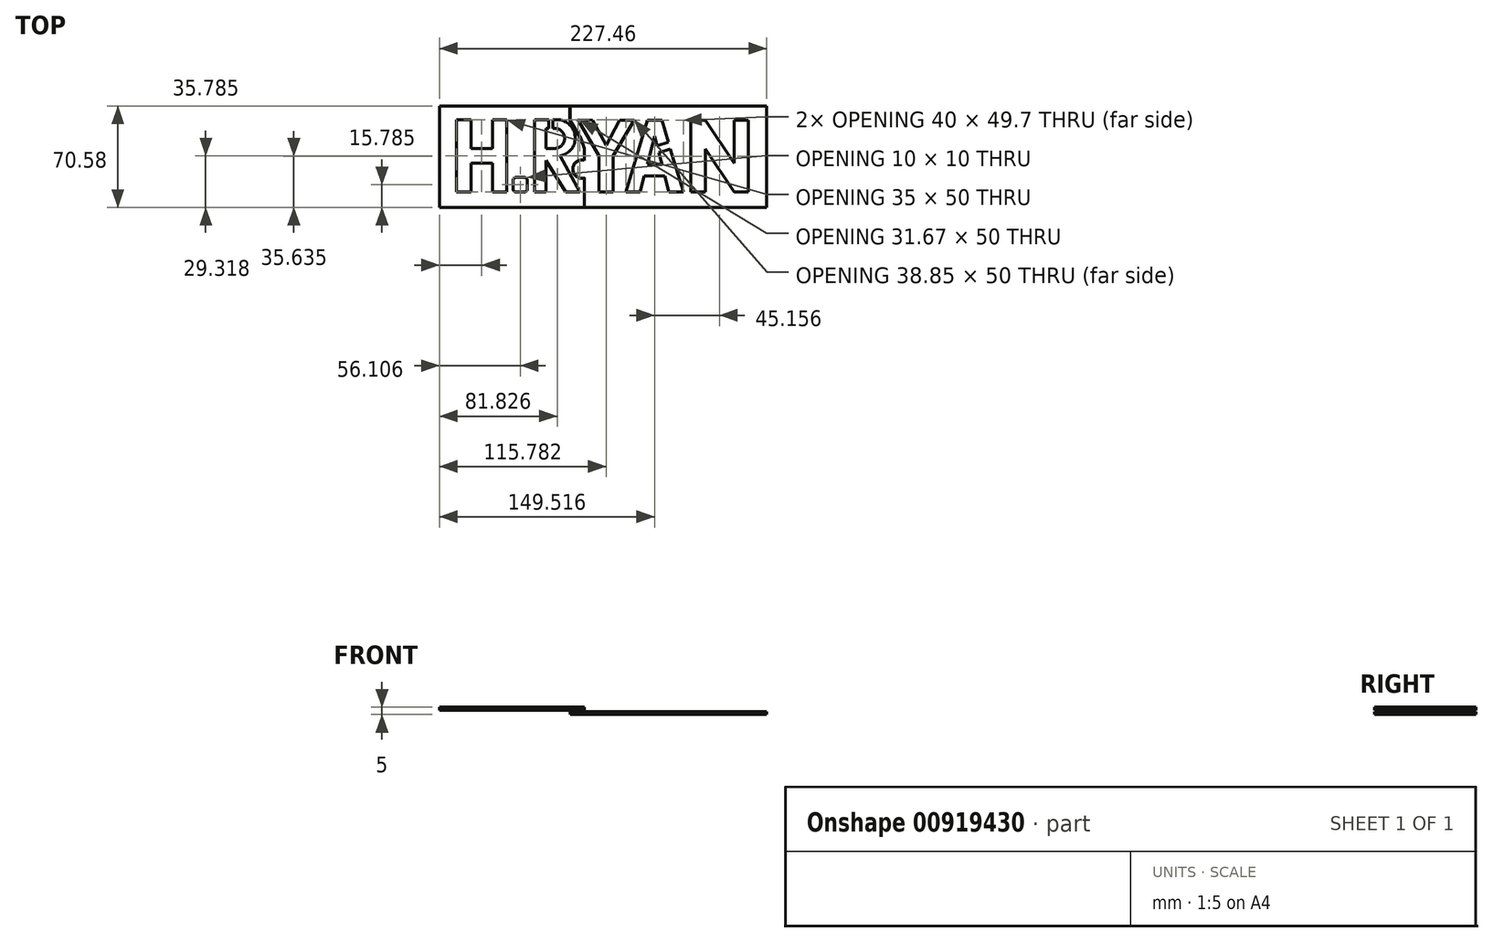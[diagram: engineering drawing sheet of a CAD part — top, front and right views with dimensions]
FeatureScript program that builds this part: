
annotation { "Feature Type Name" : "Feature", "Feature Type Description" : "" }
export const myFeature = defineFeature(function(context is Context, id is Id, definition is map)
    precondition{}
    {
        {
            var Q0;
            Q0=qCreatedBy(makeId("Top.planeOp"),FACE);
            var sketch = newSketch(context, id + "F0", { "sketchPlane" : qUnion([Q0])});
            skLineSegment(sketch, "E0", {"start": v(-56.97, 28.07) * mm, "end": v(-46.97, 28.07) * mm});
            skLineSegment(sketch, "E1", {"start": v(-56.97, 28.07) * mm, "end": v(-56.97, -21.93) * mm});
            skLineSegment(sketch, "E2", {"start": v(-56.97, -21.93) * mm, "end": v(-46.97, -21.93) * mm});
            skLineSegment(sketch, "E3", {"start": v(-46.97, -21.93) * mm, "end": v(-46.97, -1.93) * mm});
            skLineSegment(sketch, "E4", {"start": v(-46.97, 28.07) * mm, "end": v(-46.97, 8.07) * mm});
            skLineSegment(sketch, "E5", {"start": v(-46.97, 8.07) * mm, "end": v(-31.97, 8.07) * mm});
            skLineSegment(sketch, "E6", {"start": v(-46.97, -1.93) * mm, "end": v(-31.97, -1.93) * mm});
            skLineSegment(sketch, "E7", {"start": v(-31.97, -1.93) * mm, "end": v(-31.97, -21.93) * mm});
            skLineSegment(sketch, "E8", {"start": v(-31.97, -21.93) * mm, "end": v(-21.97, -21.93) * mm});
            skLineSegment(sketch, "E9", {"start": v(-21.97, -21.93) * mm, "end": v(-21.97, 28.07) * mm});
            skLineSegment(sketch, "E10", {"start": v(-21.97, 28.07) * mm, "end": v(-31.97, 28.07) * mm});
            skLineSegment(sketch, "E11", {"start": v(-31.97, 28.07) * mm, "end": v(-31.97, 8.07) * mm});
            skLineSegment(sketch, "E12", {"start": v(-15.68, -21.93) * mm, "end": v(-9.68, -21.93) * mm});
            skLineSegment(sketch, "E13", {"start": v(-7.68, -19.93) * mm, "end": v(-7.68, -13.93) * mm});
            skLineSegment(sketch, "E14", {"start": v(-9.68, -11.93) * mm, "end": v(-15.68, -11.93) * mm});
            skLineSegment(sketch, "E15", {"start": v(-17.68, -13.93) * mm, "end": v(-17.68, -19.93) * mm});
            skPoint(sketch, "E16.visualSharp", {"position": v(-17.68, -11.93) * mm});
            skArc(sketch, "E16.filletArc", {"start": v(-15.68, -11.93) * mm, "mid": v(-17.1, -12.52) * mm, "end": v(-17.68, -13.93) * mm});
            skPoint(sketch, "E17.visualSharp", {"position": v(-7.68, -11.93) * mm});
            skArc(sketch, "E17.filletArc", {"start": v(-7.68, -13.93) * mm, "mid": v(-8.27, -12.52) * mm, "end": v(-9.68, -11.93) * mm});
            skPoint(sketch, "E18.visualSharp", {"position": v(-7.68, -21.93) * mm});
            skArc(sketch, "E18.filletArc", {"start": v(-9.68, -21.93) * mm, "mid": v(-8.27, -21.35) * mm, "end": v(-7.68, -19.93) * mm});
            skPoint(sketch, "E19.visualSharp", {"position": v(-17.68, -21.93) * mm});
            skArc(sketch, "E19.filletArc", {"start": v(-17.68, -19.93) * mm, "mid": v(-17.1, -21.35) * mm, "end": v(-15.68, -21.93) * mm});
            skLineSegment(sketch, "E20", {"start": v(0, 28.07) * mm, "end": v(0, -21.93) * mm});
            skLineSegment(sketch, "E21", {"start": v(0, -21.93) * mm, "end": v(8, -21.93) * mm});
            skLineSegment(sketch, "E22", {"start": v(8, -21.93) * mm, "end": v(8, 0) * mm});
            skLineSegment(sketch, "E23", {"start": v(21.67, -21.93) * mm, "end": v(31.67, -21.93) * mm});
            skLineSegment(sketch, "E24", {"start": v(31.67, -21.93) * mm, "end": v(18, 3.07) * mm});
            skLineSegment(sketch, "E25", {"start": v(0, 28.07) * mm, "end": v(10, 28.07) * mm});
            skArc(sketch, "E26", {"start": v(18, 3.07) * mm, "mid": v(28.33, 15.57) * mm, "end": v(18, 28.07) * mm});
            skLineSegment(sketch, "E27", {"start": v(18, 28.07) * mm, "end": v(0, 28.07) * mm});
            skLineSegment(sketch, "E28", {"start": v(8, 8.24) * mm, "end": v(8, 22.3) * mm});
            skLineSegment(sketch, "E29", {"start": v(8, 22.3) * mm, "end": v(14, 22.3) * mm});
            skLineSegment(sketch, "E30", {"start": v(8, 8.24) * mm, "end": v(14, 8.24) * mm});
            skArc(sketch, "E31", {"start": v(14, 8.24) * mm, "mid": v(21.02, 15.27) * mm, "end": v(14, 22.3) * mm});
            skPoint(sketch, "E32.endSnap0", {"position": v(26.67, -21.93) * mm});
            skLineSegment(sketch, "E33", {"start": v(44.8, -21.93) * mm, "end": v(44.8, 3.07) * mm});
            skLineSegment(sketch, "E34", {"start": v(44.8, -21.93) * mm, "end": v(54.8, -21.93) * mm});
            skLineSegment(sketch, "E35", {"start": v(54.8, -21.93) * mm, "end": v(54.8, 3.07) * mm});
            skLineSegment(sketch, "E36", {"start": v(44.8, 3.07) * mm, "end": v(30.37, 28.07) * mm});
            skLineSegment(sketch, "E37", {"start": v(30.37, 28.07) * mm, "end": v(40.37, 27.91) * mm});
            skLineSegment(sketch, "E38", {"start": v(40.37, 27.91) * mm, "end": v(49.8, 10.57) * mm});
            skLineSegment(sketch, "E39", {"start": v(49.8, 27.91) * mm, "end": v(59.22, 27.76) * mm});
            skLineSegment(sketch, "E40", {"start": v(49.8, 10.57) * mm, "end": v(59.22, 27.76) * mm});
            skLineSegment(sketch, "E41", {"start": v(59.22, 27.76) * mm, "end": v(69.22, 27.76) * mm});
            skLineSegment(sketch, "E42", {"start": v(54.8, 3.07) * mm, "end": v(69.22, 27.76) * mm});
            skPoint(sketch, "E43.start.orphan", {"position": v(49.8, -21.93) * mm});
            skLineSegment(sketch, "E44", {"start": v(71.83, -21.93) * mm, "end": v(81.83, -21.93) * mm});
            skLineSegment(sketch, "E45", {"start": v(101.83, -21.93) * mm, "end": v(111.83, -21.93) * mm});
            skLineSegment(sketch, "E46", {"start": v(96.83, 27.76) * mm, "end": v(91.83, 27.76) * mm});
            skLineSegment(sketch, "E47", {"start": v(91.83, 27.76) * mm, "end": v(86.83, 27.76) * mm});
            skLineSegment(sketch, "E48", {"start": v(86.83, 27.76) * mm, "end": v(71.83, -21.93) * mm});
            skLineSegment(sketch, "E49", {"start": v(96.83, 27.76) * mm, "end": v(111.83, -21.93) * mm});
            skLineSegment(sketch, "E50", {"start": v(91.83, 16.9) * mm, "end": v(86.83, -2.52) * mm});
            skLineSegment(sketch, "E51", {"start": v(101.83, -21.93) * mm, "end": v(98.96, -10.8) * mm});
            skLineSegment(sketch, "E52", {"start": v(84.7, -10.8) * mm, "end": v(98.96, -10.8) * mm});
            skLineSegment(sketch, "E53", {"start": v(86.83, -2.52) * mm, "end": v(96.83, -2.52) * mm});
            skPoint(sketch, "E54.orphan", {"position": v(91.83, -21.93) * mm});
            skLineSegment(sketch, "E55.trimOffspring", {"start": v(84.7, -10.8) * mm, "end": v(81.83, -21.93) * mm});
            skLineSegment(sketch, "E56.trimOffspring", {"start": v(96.83, -2.52) * mm, "end": v(91.83, 16.9) * mm});
            skLineSegment(sketch, "E57", {"start": v(21.67, -21.93) * mm, "end": v(8, 0) * mm});
            skPoint(sketch, "E58.orphan", {"position": v(8, 3.07) * mm});
            skLineSegment(sketch, "E59", {"start": v(116.98, -21.93) * mm, "end": v(116.98, 27.76) * mm});
            skLineSegment(sketch, "E60", {"start": v(116.98, 27.76) * mm, "end": v(126.98, 27.76) * mm});
            skLineSegment(sketch, "E61", {"start": v(116.98, -21.93) * mm, "end": v(126.98, -21.93) * mm});
            skLineSegment(sketch, "E62", {"start": v(126.98, 7.76) * mm, "end": v(146.98, -21.93) * mm});
            skLineSegment(sketch, "E63", {"start": v(126.98, 7.76) * mm, "end": v(126.98, -21.93) * mm});
            skLineSegment(sketch, "E64", {"start": v(146.98, -1.93) * mm, "end": v(146.98, 27.76) * mm});
            skLineSegment(sketch, "E65", {"start": v(146.98, -1.93) * mm, "end": v(126.98, 27.76) * mm});
            skLineSegment(sketch, "E66", {"start": v(146.98, 27.76) * mm, "end": v(156.98, 27.76) * mm});
            skLineSegment(sketch, "E67", {"start": v(156.98, 27.76) * mm, "end": v(156.98, -21.93) * mm});
            skLineSegment(sketch, "E68", {"start": v(156.98, -21.93) * mm, "end": v(146.98, -21.93) * mm});
            skSolve(sketch);
        }
        {
            var Q0;
            Q0=makeQuery(id+"F0.imprint","IMPRINT",FACE,{"disambiguationData":[TD([[makeQuery(id+"F0.imprint","IMPRINT",EDGE,{"derivedFrom":sQuery(id+"F0.wireOp",EDGE,"E0")}),-1.0]])]});
            var Q1;
            {var subQ1=sQuery(id+"F0.wireOp",EDGE,"E20");Q1=makeQuery(id+"F0.imprint","IMPRINT",FACE,{"disambiguationData":[TD([[makeQuery(id+"F0.imprint","IMPRINT",EDGE,{"derivedFrom":subQ1}),1.0]])]});}
            var Q2;
            Q2=makeQuery(id+"F0.imprint","IMPRINT",FACE,{"disambiguationData":[TD([[makeQuery(id+"F0.imprint","IMPRINT",EDGE,{"derivedFrom":sQuery(id+"F0.wireOp",EDGE,"E12")}),1.0]])]});
            var Q3;
            Q3=makeQuery(id+"F0.imprint","IMPRINT",FACE,{"disambiguationData":[TD([[makeQuery(id+"F0.imprint","IMPRINT",EDGE,{"derivedFrom":sQuery(id+"F0.wireOp",EDGE,"E33")}),-1.0]])]});
            var Q4;
            Q4=makeQuery(id+"F0.imprint","IMPRINT",FACE,{"disambiguationData":[TD([[makeQuery(id+"F0.imprint","IMPRINT",EDGE,{"derivedFrom":sQuery(id+"F0.wireOp",EDGE,"E44")}),1.0]])]});
            var Q5;
            Q5=makeQuery(id+"F0.imprint","IMPRINT",FACE,{"disambiguationData":[TD([[makeQuery(id+"F0.imprint","IMPRINT",EDGE,{"derivedFrom":sQuery(id+"F0.wireOp",EDGE,"E59")}),-1.0]])]});
            extrude(context, id + "F1", {"entities" : qUnion([Q0, Q1, Q2, Q3, Q4, Q5]), "depth" : 25 * mm, "offsetDistance" : 25 * mm});
        }
        {
            var Q0;
            Q0=makeQuery(id+"F1.opExtrude","SWEPT_BODY",BODY,{"disambiguationData":[OSD([sQuery(id+"F0.wireOp",EDGE,"E44"),sQuery(id+"F0.wireOp",EDGE,"E45"),sQuery(id+"F0.wireOp",EDGE,"E46"),sQuery(id+"F0.wireOp",EDGE,"E47"),sQuery(id+"F0.wireOp",EDGE,"E48"),sQuery(id+"F0.wireOp",EDGE,"E49"),sQuery(id+"F0.wireOp",EDGE,"E50"),sQuery(id+"F0.wireOp",EDGE,"E51"),sQuery(id+"F0.wireOp",EDGE,"E52"),sQuery(id+"F0.wireOp",EDGE,"E53"),sQuery(id+"F0.wireOp",EDGE,"E55.trimOffspring"),sQuery(id+"F0.wireOp",EDGE,"E56.trimOffspring")])]});
            var Q1;
            Q1=makeQuery(id+"F1.opExtrude","SWEPT_BODY",BODY,{"disambiguationData":[OSD([sQuery(id+"F0.wireOp",EDGE,"E59"),sQuery(id+"F0.wireOp",EDGE,"E60"),sQuery(id+"F0.wireOp",EDGE,"E61"),sQuery(id+"F0.wireOp",EDGE,"E62"),sQuery(id+"F0.wireOp",EDGE,"E63"),sQuery(id+"F0.wireOp",EDGE,"E64"),sQuery(id+"F0.wireOp",EDGE,"E65"),sQuery(id+"F0.wireOp",EDGE,"E66"),sQuery(id+"F0.wireOp",EDGE,"E67"),sQuery(id+"F0.wireOp",EDGE,"E68")])]});
            transform(context, id + "F2", {"entities" : qUnion([Q0, Q1]), "transformType" : TransformType.TRANSLATION_3D, "dx" : -8.3 * mm, "dy" : 0 * mm, "dz" : 0 * mm, "makeCopy" : false});
        }
        {
            var Q0;
            Q0=makeQuery(id+"F1.opExtrude","SWEPT_BODY",BODY,{"disambiguationData":[OSD([sQuery(id+"F0.wireOp",EDGE,"E33"),sQuery(id+"F0.wireOp",EDGE,"E34"),sQuery(id+"F0.wireOp",EDGE,"E35"),sQuery(id+"F0.wireOp",EDGE,"E36"),sQuery(id+"F0.wireOp",EDGE,"E37"),sQuery(id+"F0.wireOp",EDGE,"E38"),sQuery(id+"F0.wireOp",EDGE,"E40"),sQuery(id+"F0.wireOp",EDGE,"E41"),sQuery(id+"F0.wireOp",EDGE,"E42")])]});
            var Q1;
            Q1=makeQuery(id+"F1.opExtrude","SWEPT_BODY",BODY,{"disambiguationData":[OSD([sQuery(id+"F0.wireOp",EDGE,"E44"),sQuery(id+"F0.wireOp",EDGE,"E45"),sQuery(id+"F0.wireOp",EDGE,"E46"),sQuery(id+"F0.wireOp",EDGE,"E47"),sQuery(id+"F0.wireOp",EDGE,"E48"),sQuery(id+"F0.wireOp",EDGE,"E49"),sQuery(id+"F0.wireOp",EDGE,"E50"),sQuery(id+"F0.wireOp",EDGE,"E51"),sQuery(id+"F0.wireOp",EDGE,"E52"),sQuery(id+"F0.wireOp",EDGE,"E53"),sQuery(id+"F0.wireOp",EDGE,"E55.trimOffspring"),sQuery(id+"F0.wireOp",EDGE,"E56.trimOffspring")])]});
            var Q2;
            Q2=makeQuery(id+"F1.opExtrude","SWEPT_BODY",BODY,{"disambiguationData":[OSD([sQuery(id+"F0.wireOp",EDGE,"E59"),sQuery(id+"F0.wireOp",EDGE,"E60"),sQuery(id+"F0.wireOp",EDGE,"E61"),sQuery(id+"F0.wireOp",EDGE,"E62"),sQuery(id+"F0.wireOp",EDGE,"E63"),sQuery(id+"F0.wireOp",EDGE,"E64"),sQuery(id+"F0.wireOp",EDGE,"E65"),sQuery(id+"F0.wireOp",EDGE,"E66"),sQuery(id+"F0.wireOp",EDGE,"E67"),sQuery(id+"F0.wireOp",EDGE,"E68")])]});
            var Q3;
            Q3=makeQuery(id+"F1.opExtrude","SWEPT_BODY",BODY,{"disambiguationData":[OSD([sQuery(id+"F0.wireOp",EDGE,"E20"),sQuery(id+"F0.wireOp",EDGE,"E21"),sQuery(id+"F0.wireOp",EDGE,"E22"),sQuery(id+"F0.wireOp",EDGE,"E23"),sQuery(id+"F0.wireOp",EDGE,"E24"),sQuery(id+"F0.wireOp",EDGE,"E26"),sQuery(id+"F0.wireOp",EDGE,"E27"),sQuery(id+"F0.wireOp",EDGE,"E28"),sQuery(id+"F0.wireOp",EDGE,"E29"),sQuery(id+"F0.wireOp",EDGE,"E30"),sQuery(id+"F0.wireOp",EDGE,"E31"),sQuery(id+"F0.wireOp",EDGE,"E57")])]});
            transform(context, id + "F3", {"entities" : qUnion([Q0, Q1, Q2, Q3]), "transformType" : TransformType.TRANSLATION_3D, "dx" : -2.8 * mm, "dy" : 0 * mm, "dz" : 0 * mm, "makeCopy" : false});
        }
        {
            var Q0;
            Q0=qCreatedBy(makeId("Top.planeOp"),FACE);
            var sketch = newSketch(context, id + "F4", { "sketchPlane" : qUnion([Q0])});
            skLineSegment(sketch, "E69.bottom", {"start": v(-68.8, 37.86) * mm, "end": v(158.67, 37.86) * mm});
            skLineSegment(sketch, "E69.top", {"start": v(-68.8, -32.72) * mm, "end": v(158.67, -32.72) * mm});
            skLineSegment(sketch, "E69.left", {"start": v(-68.8, 37.86) * mm, "end": v(-68.8, -32.72) * mm});
            skLineSegment(sketch, "E69.right", {"start": v(158.67, 37.86) * mm, "end": v(158.67, -32.72) * mm});
            skSolve(sketch);
        }
        {
            var Q0;
            Q0=makeQuery(id+"F4.imprint","IMPRINT",FACE,{"disambiguationData":[TD([[makeQuery(id+"F4.imprint","IMPRINT",EDGE,{"derivedFrom":sQuery(id+"F4.wireOp",EDGE,"E69.bottom")}),-1.0]])]});
            extrude(context, id + "F5", {"entities" : qUnion([Q0]), "operationType" : NewBodyOperationType.ADD, "depth" : 20 * mm, "offsetDistance" : 25 * mm});
        }
        {
            var Q0;
            Q0=makeQuery(id+"F1.opExtrude","CAP_FACE",FACE,{"disambiguationData":[OSD([sQuery(id+"F0.wireOp",EDGE,"E0"),sQuery(id+"F0.wireOp",EDGE,"E1"),sQuery(id+"F0.wireOp",EDGE,"E2"),sQuery(id+"F0.wireOp",EDGE,"E3"),sQuery(id+"F0.wireOp",EDGE,"E4"),sQuery(id+"F0.wireOp",EDGE,"E5"),sQuery(id+"F0.wireOp",EDGE,"E6"),sQuery(id+"F0.wireOp",EDGE,"E7"),sQuery(id+"F0.wireOp",EDGE,"E8"),sQuery(id+"F0.wireOp",EDGE,"E9"),sQuery(id+"F0.wireOp",EDGE,"E10"),sQuery(id+"F0.wireOp",EDGE,"E11")])],"isStart":false});
            var Q1;
            Q1=makeQuery(id+"F1.opExtrude","CAP_FACE",FACE,{"disambiguationData":[OSD([sQuery(id+"F0.wireOp",EDGE,"E12"),sQuery(id+"F0.wireOp",EDGE,"E13"),sQuery(id+"F0.wireOp",EDGE,"E14"),sQuery(id+"F0.wireOp",EDGE,"E15"),sQuery(id+"F0.wireOp",EDGE,"E16.filletArc"),sQuery(id+"F0.wireOp",EDGE,"E17.filletArc"),sQuery(id+"F0.wireOp",EDGE,"E18.filletArc"),sQuery(id+"F0.wireOp",EDGE,"E19.filletArc")])],"isStart":false});
            var Q2;
            Q2=makeQuery(id+"F1.opExtrude","CAP_FACE",FACE,{"disambiguationData":[OSD([sQuery(id+"F0.wireOp",EDGE,"E20"),sQuery(id+"F0.wireOp",EDGE,"E21"),sQuery(id+"F0.wireOp",EDGE,"E22"),sQuery(id+"F0.wireOp",EDGE,"E23"),sQuery(id+"F0.wireOp",EDGE,"E24"),sQuery(id+"F0.wireOp",EDGE,"E26"),sQuery(id+"F0.wireOp",EDGE,"E27"),sQuery(id+"F0.wireOp",EDGE,"E28"),sQuery(id+"F0.wireOp",EDGE,"E29"),sQuery(id+"F0.wireOp",EDGE,"E30"),sQuery(id+"F0.wireOp",EDGE,"E31"),sQuery(id+"F0.wireOp",EDGE,"E57")])],"isStart":false});
            var Q3;
            Q3=makeQuery(id+"F1.opExtrude","CAP_FACE",FACE,{"disambiguationData":[OSD([sQuery(id+"F0.wireOp",EDGE,"E33"),sQuery(id+"F0.wireOp",EDGE,"E34"),sQuery(id+"F0.wireOp",EDGE,"E35"),sQuery(id+"F0.wireOp",EDGE,"E36"),sQuery(id+"F0.wireOp",EDGE,"E37"),sQuery(id+"F0.wireOp",EDGE,"E38"),sQuery(id+"F0.wireOp",EDGE,"E40"),sQuery(id+"F0.wireOp",EDGE,"E41"),sQuery(id+"F0.wireOp",EDGE,"E42")])],"isStart":false});
            var Q4;
            Q4=makeQuery(id+"F1.opExtrude","CAP_FACE",FACE,{"disambiguationData":[OSD([sQuery(id+"F0.wireOp",EDGE,"E44"),sQuery(id+"F0.wireOp",EDGE,"E45"),sQuery(id+"F0.wireOp",EDGE,"E46"),sQuery(id+"F0.wireOp",EDGE,"E47"),sQuery(id+"F0.wireOp",EDGE,"E48"),sQuery(id+"F0.wireOp",EDGE,"E49"),sQuery(id+"F0.wireOp",EDGE,"E50"),sQuery(id+"F0.wireOp",EDGE,"E51"),sQuery(id+"F0.wireOp",EDGE,"E52"),sQuery(id+"F0.wireOp",EDGE,"E53"),sQuery(id+"F0.wireOp",EDGE,"E55.trimOffspring"),sQuery(id+"F0.wireOp",EDGE,"E56.trimOffspring")])],"isStart":false});
            var Q5;
            Q5=makeQuery(id+"F1.opExtrude","CAP_FACE",FACE,{"disambiguationData":[OSD([sQuery(id+"F0.wireOp",EDGE,"E59"),sQuery(id+"F0.wireOp",EDGE,"E60"),sQuery(id+"F0.wireOp",EDGE,"E61"),sQuery(id+"F0.wireOp",EDGE,"E62"),sQuery(id+"F0.wireOp",EDGE,"E63"),sQuery(id+"F0.wireOp",EDGE,"E64"),sQuery(id+"F0.wireOp",EDGE,"E65"),sQuery(id+"F0.wireOp",EDGE,"E66"),sQuery(id+"F0.wireOp",EDGE,"E67"),sQuery(id+"F0.wireOp",EDGE,"E68")])],"isStart":false});
            extrude(context, id + "F6", {"entities" : qUnion([Q0, Q1, Q2, Q3, Q4, Q5]), "operationType" : NewBodyOperationType.REMOVE, "oppositeDirection" : true, "depth" : 60.1 * mm, "offsetDistance" : 25 * mm});
        }
        {
            var Q0;
            Q0=qCreatedBy(makeId("Top.planeOp"),FACE);
            var sketch = newSketch(context, id + "F7", { "sketchPlane" : qUnion([Q0])});
            skLineSegment(sketch, "E70.bottom", {"start": v(6.98, 21.3) * mm, "end": v(9.83, 21.3) * mm});
            skLineSegment(sketch, "E70.top", {"start": v(6.98, 29.58) * mm, "end": v(9.83, 29.58) * mm});
            skLineSegment(sketch, "E70.left", {"start": v(6.98, 21.3) * mm, "end": v(6.98, 29.58) * mm});
            skLineSegment(sketch, "E70.right", {"start": v(9.83, 21.3) * mm, "end": v(9.83, 29.58) * mm});
            skLineSegment(sketch, "E71", {"start": v(81.95, 9.96) * mm, "end": v(92.34, 13.37) * mm});
            skLineSegment(sketch, "E72", {"start": v(92.34, 13.37) * mm, "end": v(93.87, 8.71) * mm});
            skLineSegment(sketch, "E73", {"start": v(93.87, 8.71) * mm, "end": v(82.32, 4.93) * mm});
            skLineSegment(sketch, "E74", {"start": v(82.32, 4.93) * mm, "end": v(81.95, 9.96) * mm});
            skSolve(sketch);
        }
        {
            var Q0;
            Q0=makeQuery(id+"F7.imprint","IMPRINT",FACE,{"disambiguationData":[TD([[makeQuery(id+"F7.imprint","IMPRINT",EDGE,{"derivedFrom":sQuery(id+"F7.wireOp",EDGE,"E70.bottom")}),1.0]])]});
            var Q1;
            Q1=makeQuery(id+"F7.imprint","IMPRINT",FACE,{"disambiguationData":[TD([[makeQuery(id+"F7.imprint","IMPRINT",EDGE,{"derivedFrom":sQuery(id+"F7.wireOp",EDGE,"E71")}),-1.0]])]});
            extrude(context, id + "F8", {"entities" : qUnion([Q0, Q1]), "operationType" : NewBodyOperationType.ADD, "depth" : 20 * mm, "offsetDistance" : 25 * mm});
        }
        {
            var Q0;
            {var subQ0=sQuery(id+"F4.wireOp",EDGE,"E69.bottom");var subQ1=sQuery(id+"F4.wireOp",EDGE,"E69.top");var subQ2=sQuery(id+"F4.wireOp",EDGE,"E69.left");var subQ3=sQuery(id+"F4.wireOp",EDGE,"E69.right");var subQ4=makeQuery(id+"F5.opExtrude","CAP_FACE",FACE,{"disambiguationData":[OSD([subQ0,subQ1,subQ2,subQ3])],"isStart":false});Q0=makeQuery(id+"F8.boolean.opBoolean","MERGE",FACE,{"derivedFrom":[makeQuery(id+"F5.boolean.opBoolean","SPLIT",FACE,{"disambiguationData":[TD([makeQuery(id+"F1.opExtrude","SWEPT_FACE",FACE,{"disambiguationData":[OSD([sQuery(id+"F0.wireOp",EDGE,"E50")])]})])],"derivedFrom":subQ4}),makeQuery(id+"F5.boolean.opBoolean","SPLIT",FACE,{"disambiguationData":[TD([makeQuery(id+"F1.opExtrude","SWEPT_FACE",FACE,{"disambiguationData":[OSD([sQuery(id+"F0.wireOp",EDGE,"E28")])]})])],"derivedFrom":subQ4}),makeQuery(id+"F5.boolean.opBoolean","SPLIT",FACE,{"disambiguationData":[TD([makeQuery(id+"F1.opExtrude","SWEPT_FACE",FACE,{"disambiguationData":[OSD([sQuery(id+"F0.wireOp",EDGE,"E0")])]})])],"derivedFrom":subQ4}),makeQuery(id+"F8.opExtrude","CAP_FACE",FACE,{"disambiguationData":[OSD([sQuery(id+"F7.wireOp",EDGE,"E70.bottom"),sQuery(id+"F7.wireOp",EDGE,"E70.top"),sQuery(id+"F7.wireOp",EDGE,"E70.left"),sQuery(id+"F7.wireOp",EDGE,"E70.right")])],"isStart":false}),makeQuery(id+"F8.opExtrude","CAP_FACE",FACE,{"disambiguationData":[OSD([sQuery(id+"F7.wireOp",EDGE,"E71"),sQuery(id+"F7.wireOp",EDGE,"E72"),sQuery(id+"F7.wireOp",EDGE,"E73"),sQuery(id+"F7.wireOp",EDGE,"E74")])],"isStart":false})]});}
            extrude(context, id + "F9", {"entities" : qUnion([Q0]), "operationType" : NewBodyOperationType.REMOVE, "oppositeDirection" : true, "depth" : 18 * mm, "offsetDistance" : 25 * mm});
        }
        {
            var Q0;
            Q0=makeQuery(id+"F9.boolean.opBoolean","COPY",FACE,{"derivedFrom":makeQuery(id+"F9.opExtrude","CAP_FACE",FACE,{"disambiguationData":[OSD([sQuery(id+"F4.wireOp",EDGE,"E69.bottom"),sQuery(id+"F4.wireOp",EDGE,"E69.top"),sQuery(id+"F4.wireOp",EDGE,"E69.left"),sQuery(id+"F4.wireOp",EDGE,"E69.right"),sQuery(id+"F7.wireOp",EDGE,"E70.bottom"),sQuery(id+"F7.wireOp",EDGE,"E70.top"),sQuery(id+"F7.wireOp",EDGE,"E70.left"),sQuery(id+"F7.wireOp",EDGE,"E70.right"),sQuery(id+"F7.wireOp",EDGE,"E71"),sQuery(id+"F7.wireOp",EDGE,"E72"),sQuery(id+"F7.wireOp",EDGE,"E73"),sQuery(id+"F7.wireOp",EDGE,"E74")])],"isStart":false})});
            var sketch = newSketch(context, id + "F10", { "sketchPlane" : qUnion([Q0])});
            skLineSegment(sketch, "E75", {"start": v(21.91, 37.86) * mm, "end": v(21.91, 28.07) * mm});
            skLineSegment(sketch, "E76", {"start": v(21.91, 28.07) * mm, "end": v(29.68, 14.6) * mm});
            skLineSegment(sketch, "E77", {"start": v(29.68, 14.6) * mm, "end": v(31.94, 8.24) * mm});
            skLineSegment(sketch, "E78", {"start": v(31.94, 8.24) * mm, "end": v(31.94, 0) * mm});
            skArc(sketch, "E79", {"start": v(31.94, 0) * mm, "mid": v(23.93, -6.12) * mm, "end": v(31.94, -12.24) * mm});
            skLineSegment(sketch, "E80.trimOffspring", {"start": v(31.94, -12.24) * mm, "end": v(31.94, -32.72) * mm});
            skSolve(sketch);
        }
        {
            var Q0;
            {var subQ8=sQuery(id+"F10.wireOp",EDGE,"E75");Q0=makeQuery(id+"F10.imprint","IMPRINT",FACE,{"disambiguationData":[TD([[makeQuery(id+"F10.imprint","IMPRINT",EDGE,{"derivedFrom":subQ8}),1.0]])]});}
            extrude(context, id + "F11", {"entities" : qUnion([Q0]), "operationType" : NewBodyOperationType.ADD, "oppositeDirection" : true, "depth" : 5 * mm, "offsetDistance" : 25 * mm});
        }
        {
            var Q0;
            {var subQ0=sQuery(id+"F4.wireOp",EDGE,"E69.right");Q0=makeQuery(id+"F11.boolean.opBoolean","MERGE",FACE,{"derivedFrom":[makeQuery(id+"F5.opExtrude","SWEPT_FACE",FACE,{"disambiguationData":[OSD([subQ0])]}),makeQuery(id+"F11.opExtrude","SWEPT_FACE",FACE,{"disambiguationData":[OSD([subQ0])]})]});}
            var sketch = newSketch(context, id + "F12", { "sketchPlane" : qUnion([Q0])});
            skLineSegment(sketch, "E81", {"start": v(37.86, -3) * mm, "end": v(37.86, -1) * mm});
            skLineSegment(sketch, "E82", {"start": v(37.86, 2) * mm, "end": v(37.86, 0) * mm});
            skLineSegment(sketch, "E83", {"start": v(37.86, -1) * mm, "end": v(-32.72, -1) * mm});
            skLineSegment(sketch, "E84", {"start": v(37.86, 0) * mm, "end": v(-32.72, 0) * mm});
            skSolve(sketch);
        }
        {
            var Q0;
            {var subQ0=sQuery(id+"F12.wireOp",EDGE,"E83");Q0=makeQuery(id+"F12.imprint","IMPRINT",FACE,{"disambiguationData":[TD([[makeQuery(id+"F12.imprint","IMPRINT",EDGE,{"derivedFrom":subQ0}),-1.0]])]});}
            extrude(context, id + "F13", {"entities" : qUnion([Q0]), "operationType" : NewBodyOperationType.REMOVE, "oppositeDirection" : true, "depth" : 150.9 * mm, "offsetDistance" : 25 * mm});
        }
        {
            var Q0;
            {var subQ0=sQuery(id+"F0.wireOp",EDGE,"E51");var subQ1=sQuery(id+"F0.wireOp",EDGE,"E48");var subQ2=sQuery(id+"F0.wireOp",EDGE,"E47");var subQ3=sQuery(id+"F0.wireOp",EDGE,"E46");var subQ4=sQuery(id+"F0.wireOp",EDGE,"E45");var subQ5=sQuery(id+"F0.wireOp",EDGE,"E44");var subQ6=sQuery(id+"F0.wireOp",EDGE,"E42");var subQ7=sQuery(id+"F0.wireOp",EDGE,"E41");var subQ8=sQuery(id+"F0.wireOp",EDGE,"E40");var subQ9=sQuery(id+"F0.wireOp",EDGE,"E38");var subQ10=sQuery(id+"F0.wireOp",EDGE,"E37");var subQ11=sQuery(id+"F0.wireOp",EDGE,"E36");var subQ12=sQuery(id+"F0.wireOp",EDGE,"E35");var subQ13=sQuery(id+"F0.wireOp",EDGE,"E34");var subQ14=sQuery(id+"F0.wireOp",EDGE,"E33");var subQ15=sQuery(id+"F0.wireOp",EDGE,"E27");var subQ16=sQuery(id+"F0.wireOp",EDGE,"E26");var subQ17=sQuery(id+"F0.wireOp",EDGE,"E24");var subQ18=sQuery(id+"F0.wireOp",EDGE,"E23");var subQ19=sQuery(id+"F0.wireOp",EDGE,"E22");var subQ20=sQuery(id+"F0.wireOp",EDGE,"E21");var subQ21=sQuery(id+"F0.wireOp",EDGE,"E20");var subQ22=sQuery(id+"F0.wireOp",EDGE,"E19.filletArc");var subQ23=sQuery(id+"F0.wireOp",EDGE,"E18.filletArc");var subQ24=sQuery(id+"F0.wireOp",EDGE,"E5");var subQ25=sQuery(id+"F0.wireOp",EDGE,"E49");var subQ26=sQuery(id+"F4.wireOp",EDGE,"E69.bottom");var subQ27=sQuery(id+"F0.wireOp",EDGE,"E4");var subQ28=sQuery(id+"F0.wireOp",EDGE,"E3");var subQ29=sQuery(id+"F0.wireOp",EDGE,"E2");var subQ30=sQuery(id+"F4.wireOp",EDGE,"E69.right");var subQ31=sQuery(id+"F0.wireOp",EDGE,"E10");var subQ32=sQuery(id+"F0.wireOp",EDGE,"E0");var subQ33=sQuery(id+"F4.wireOp",EDGE,"E69.top");var subQ34=sQuery(id+"F0.wireOp",EDGE,"E8");var subQ35=sQuery(id+"F0.wireOp",EDGE,"E1");var subQ36=sQuery(id+"F4.wireOp",EDGE,"E69.left");var subQ37=sQuery(id+"F0.wireOp",EDGE,"E9");var subQ38=sQuery(id+"F0.wireOp",EDGE,"E6");var subQ39=sQuery(id+"F0.wireOp",EDGE,"E7");var subQ40=sQuery(id+"F0.wireOp",EDGE,"E11");var subQ41=sQuery(id+"F0.wireOp",EDGE,"E12");var subQ42=sQuery(id+"F0.wireOp",EDGE,"E13");var subQ43=sQuery(id+"F0.wireOp",EDGE,"E14");var subQ44=sQuery(id+"F0.wireOp",EDGE,"E15");var subQ45=sQuery(id+"F0.wireOp",EDGE,"E16.filletArc");var subQ46=sQuery(id+"F0.wireOp",EDGE,"E17.filletArc");var subQ47=sQuery(id+"F0.wireOp",EDGE,"E52");var subQ48=sQuery(id+"F0.wireOp",EDGE,"E55.trimOffspring");var subQ49=sQuery(id+"F0.wireOp",EDGE,"E57");var subQ50=sQuery(id+"F0.wireOp",EDGE,"E59");var subQ51=sQuery(id+"F0.wireOp",EDGE,"E60");var subQ52=sQuery(id+"F0.wireOp",EDGE,"E61");var subQ53=sQuery(id+"F0.wireOp",EDGE,"E62");var subQ54=sQuery(id+"F0.wireOp",EDGE,"E63");var subQ55=sQuery(id+"F0.wireOp",EDGE,"E64");var subQ56=sQuery(id+"F0.wireOp",EDGE,"E65");var subQ57=sQuery(id+"F0.wireOp",EDGE,"E66");var subQ58=sQuery(id+"F0.wireOp",EDGE,"E67");var subQ59=sQuery(id+"F0.wireOp",EDGE,"E68");var subQ60=sQuery(id+"F0.wireOp",EDGE,"E56.trimOffspring");var subQ61=sQuery(id+"F0.wireOp",EDGE,"E53");var subQ62=sQuery(id+"F0.wireOp",EDGE,"E50");var subQ63=sQuery(id+"F0.wireOp",EDGE,"E31");var subQ64=sQuery(id+"F0.wireOp",EDGE,"E30");var subQ65=sQuery(id+"F0.wireOp",EDGE,"E29");var subQ66=sQuery(id+"F0.wireOp",EDGE,"E28");var subQ67=makeQuery(id+"F5.boolean.opBoolean","MERGE",FACE,{"derivedFrom":[makeQuery(id+"F1.opExtrude","CAP_FACE",FACE,{"disambiguationData":[OSD([subQ32,subQ35,subQ29,subQ28,subQ27,subQ24,subQ38,subQ39,subQ34,subQ37,subQ31,subQ40])],"isStart":true}),makeQuery(id+"F1.opExtrude","CAP_FACE",FACE,{"disambiguationData":[OSD([subQ41,subQ42,subQ43,subQ44,subQ45,subQ46,subQ23,subQ22])],"isStart":true}),makeQuery(id+"F1.opExtrude","CAP_FACE",FACE,{"disambiguationData":[OSD([subQ21,subQ20,subQ19,subQ18,subQ17,subQ16,subQ15,subQ66,subQ65,subQ64,subQ63,subQ49])],"isStart":true}),makeQuery(id+"F1.opExtrude","CAP_FACE",FACE,{"disambiguationData":[OSD([subQ14,subQ13,subQ12,subQ11,subQ10,subQ9,subQ8,subQ7,subQ6])],"isStart":true}),makeQuery(id+"F1.opExtrude","CAP_FACE",FACE,{"disambiguationData":[OSD([subQ5,subQ4,subQ3,subQ2,subQ1,subQ25,subQ62,subQ0,subQ47,subQ61,subQ48,subQ60])],"isStart":true}),makeQuery(id+"F1.opExtrude","CAP_FACE",FACE,{"disambiguationData":[OSD([subQ50,subQ51,subQ52,subQ53,subQ54,subQ55,subQ56,subQ57,subQ58,subQ59])],"isStart":true}),makeQuery(id+"F5.opExtrude","CAP_FACE",FACE,{"disambiguationData":[OSD([subQ26,subQ33,subQ36,subQ30])],"isStart":true})]});Q0=makeQuery(id+"F13.boolean.opBoolean","MERGE",FACE,{"derivedFrom":[makeQuery(id+"F8.boolean.opBoolean","MERGE",FACE,{"derivedFrom":[makeQuery(id+"F6.boolean.opBoolean","SPLIT",FACE,{"disambiguationData":[TD([makeQuery(id+"F6.opExtrude","SWEPT_FACE",FACE,{"disambiguationData":[OSD([subQ62])]})])],"derivedFrom":subQ67}),makeQuery(id+"F6.boolean.opBoolean","SPLIT",FACE,{"disambiguationData":[TD([makeQuery(id+"F6.opExtrude","SWEPT_FACE",FACE,{"disambiguationData":[OSD([subQ66])]})])],"derivedFrom":subQ67}),makeQuery(id+"F6.boolean.opBoolean","SPLIT",FACE,{"disambiguationData":[TD([makeQuery(id+"F5.opExtrude","SWEPT_FACE",FACE,{"disambiguationData":[OSD([subQ26])]})])],"derivedFrom":subQ67}),makeQuery(id+"F8.opExtrude","CAP_FACE",FACE,{"disambiguationData":[OSD([sQuery(id+"F7.wireOp",EDGE,"E70.bottom"),sQuery(id+"F7.wireOp",EDGE,"E70.top"),sQuery(id+"F7.wireOp",EDGE,"E70.left"),sQuery(id+"F7.wireOp",EDGE,"E70.right")])],"isStart":true}),makeQuery(id+"F8.opExtrude","CAP_FACE",FACE,{"disambiguationData":[OSD([sQuery(id+"F7.wireOp",EDGE,"E71"),sQuery(id+"F7.wireOp",EDGE,"E72"),sQuery(id+"F7.wireOp",EDGE,"E73"),sQuery(id+"F7.wireOp",EDGE,"E74")])],"isStart":true})]})],"fromTools":[makeQuery(id+"F13.opExtrude","SWEPT_FACE",FACE,{"disambiguationData":[OSD([sQuery(id+"F12.wireOp",EDGE,"E84")])]})]});}
            var sketch = newSketch(context, id + "F14", { "sketchPlane" : qUnion([Q0])});
            skLineSegment(sketch, "E85", {"start": v(21.85, -37.86) * mm, "end": v(21.85, -28.2) * mm});
            skLineSegment(sketch, "E86", {"start": v(21.85, -28.2) * mm, "end": v(29.62, -14.73) * mm});
            skLineSegment(sketch, "E87", {"start": v(29.62, -14.73) * mm, "end": v(31.93, -8.25) * mm});
            skLineSegment(sketch, "E88", {"start": v(31.93, -8.25) * mm, "end": v(31.93, 0) * mm});
            skArc(sketch, "E89", {"start": v(31.93, 12.15) * mm, "mid": v(23.8, 6.08) * mm, "end": v(31.93, 0) * mm});
            skLineSegment(sketch, "E90", {"start": v(31.93, 12.15) * mm, "end": v(31.93, 32.72) * mm});
            skSolve(sketch);
        }
        {
            var Q0;
            {var subQ22=sQuery(id+"F14.wireOp",EDGE,"E85");Q0=makeQuery(id+"F14.imprint","IMPRINT",FACE,{"disambiguationData":[TD([[makeQuery(id+"F14.imprint","IMPRINT",EDGE,{"derivedFrom":subQ22}),-1.0]])]});}
            extrude(context, id + "F15", {"entities" : qUnion([Q0]), "operationType" : NewBodyOperationType.REMOVE, "oppositeDirection" : true, "depth" : 25 * mm, "offsetDistance" : 25 * mm});
        }
    });
